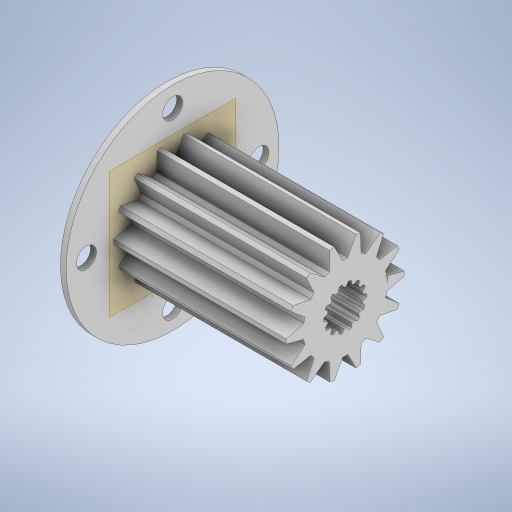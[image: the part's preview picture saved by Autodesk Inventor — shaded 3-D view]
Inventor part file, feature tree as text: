
AUTODESK INVENTOR PART (.ipt)
format: ipt  version: 2023 (Build 270158000, 158)  size: 467,456 bytes
history: native  units: mm
features: sketch x3, extrude x3, plane x2
ambient origin geometry x8: Origin, YZ Plane, XZ Plane, XY Plane, X Axis, Y Axis, Z Axis, Center Point
bodies: Solid1 (feature_tree)
feature tree (8):
  sketch  "Sketch1"  dims[d0=30.0mm d1=3.5mm]
  plane  "Work Plane1"
  plane  "Work Plane2"
  extrude  "Extrusion2"  Depth=30.0mm
  extrude  "Extrusion3"  Depth=37.0mm
  extrude  "Extrusion4"  TaperAngle=360.0deg  [1 undecoded]
  sketch  "Sketch3"  dims[d10=140.0mm d11=360.0deg d12=14.6304mm d14=1.168mm d15=3.0226mm d16=2.584833mm d17=140.0mm d19=360.0deg d21=30.0mm d22=0.0mm d23=30.0mm d24=0.0mm d25=3.5mm d26=1.0mm d27=0.0mm]
  sketch  "Sketch2"  dims[d2=40.0mm d4=360.0deg d6=37.0mm]
note: 1 required parameter value undecoded (feature->parameter linkage not recoverable at this tier; creation-order binding heuristic only, values carry confidence <= 0.55)
